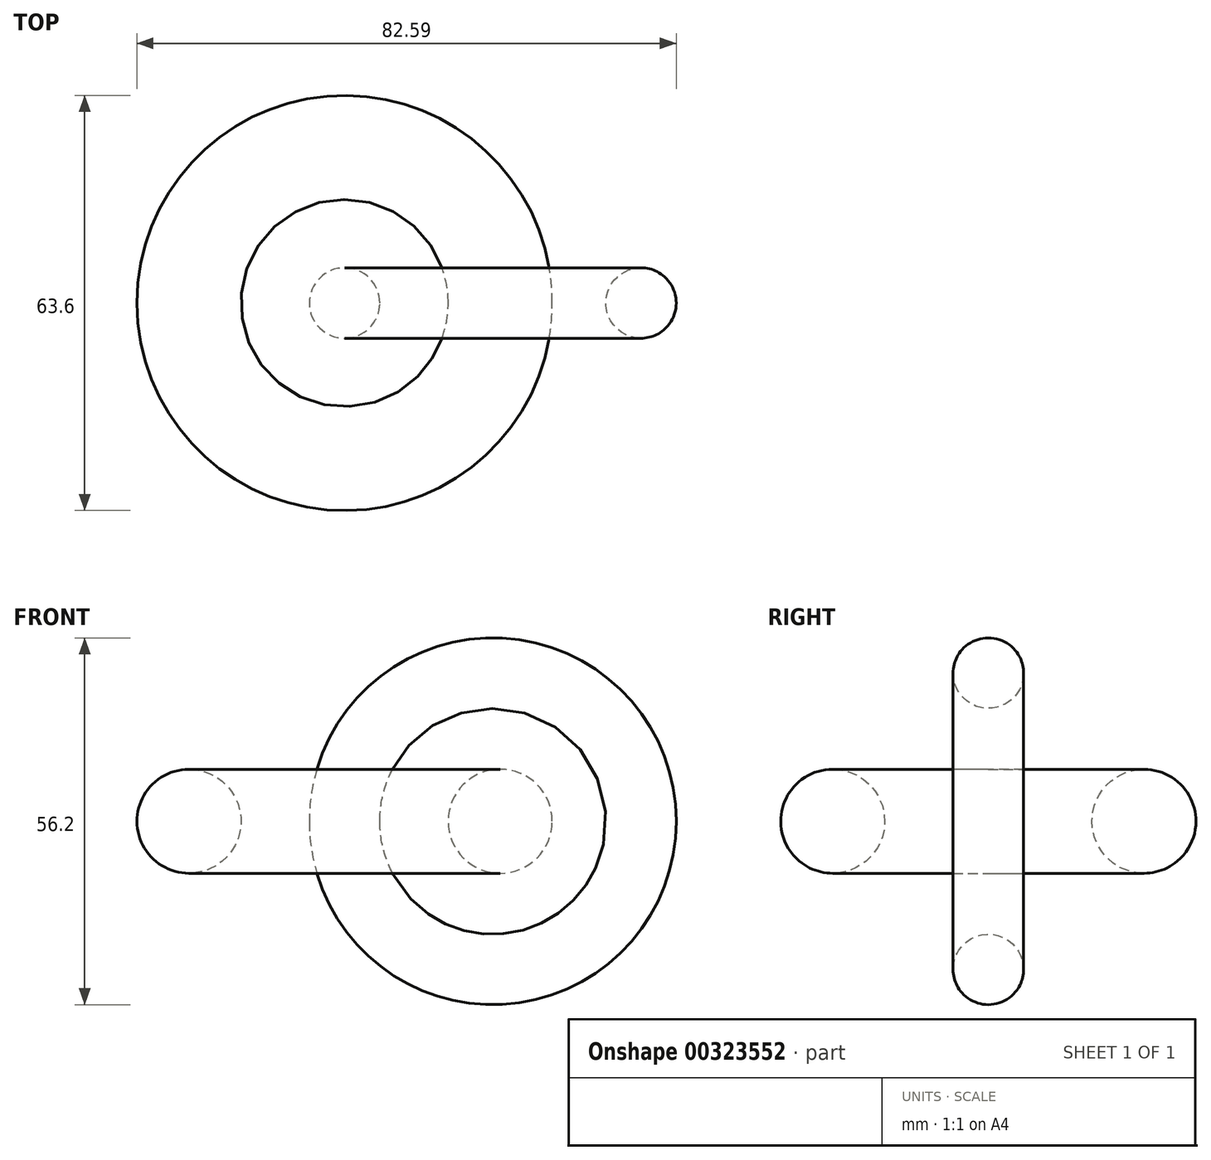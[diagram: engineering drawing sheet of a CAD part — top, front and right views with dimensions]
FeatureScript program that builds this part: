
annotation { "Feature Type Name" : "Feature", "Feature Type Description" : "" }
export const myFeature = defineFeature(function(context is Context, id is Id, definition is map)
    precondition{}
    {
        {
            var Q0;
            Q0=qCreatedBy(makeId("Front.planeOp"),FACE);
            var sketch = newSketch(context, id + "F0", { "sketchPlane" : qUnion([Q0])});
            skCircle(sketch, "E0", {"center": v(-23.83, 0) * mm, "radius": 7.96 * mm});
            skLineSegment(sketch, "E1", {"start": v(0, 37.74) * mm, "end": v(0, -39.15) * mm, "construction": true});
            skSolve(sketch);
        }
        {
            var Q0;
            Q0=makeQuery(id+"F0.imprint","IMPRINT",FACE,{"disambiguationData":[TD([[makeQuery(id+"F0.imprint","IMPRINT",EDGE,{"derivedFrom":sQuery(id+"F0.wireOp",EDGE,"E0")}),1.0]])]});
            var Q1;
            Q1=sQuery(id+"F0.wireOp",EDGE,"E1");
            revolve(context, id + "F1", {"entities" : qUnion([Q0]), "axis" : qUnion([Q1]), "revolveType" : RevolveType.FULL});
        }
        {
            var Q0;
            Q0=qCreatedBy(makeId("Top.planeOp"),FACE);
            var sketch = newSketch(context, id + "F2", { "sketchPlane" : qUnion([Q0])});
            skCircle(sketch, "E2", {"center": v(0, 0) * mm, "radius": 5.4 * mm});
            skLineSegment(sketch, "E3", {"start": v(22.7, 40.86) * mm, "end": v(22.7, -47.67) * mm, "construction": true});
            skSolve(sketch);
        }
        {
            var Q0;
            Q0 = qSketchRegion(id + "F2", true);
            var Q1;
            Q1=sQuery(id+"F2.wireOp",EDGE,"E3");
            revolve(context, id + "F3", {"entities" : qUnion([Q0]), "axis" : qUnion([Q1]), "revolveType" : RevolveType.FULL});
        }
    });
